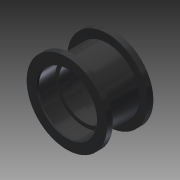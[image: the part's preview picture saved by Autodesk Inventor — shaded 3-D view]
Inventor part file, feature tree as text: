
AUTODESK INVENTOR PART (.ipt)
format: ipt  version: 2014 SP1 (Build 180222100, 222)  size: 124,416 bytes
history: native  units: in
note: dims shown in document units (in); Inventor stores cm internally (conversion verified against a paired STEP export)
features: revolve x1, chamfer x1, sketch x1
ambient origin geometry x8: Origin, YZ Plane, XZ Plane, XY Plane, X Axis, Y Axis, Z Axis, Center Point
bodies: Solid1 (feature_tree)
feature tree (3):
  revolve  "Revolution1"  [1 undecoded]
  chamfer  "Chamfer1"  Distance=0.5469in
  sketch  "Sketch1"  dims[d0=0.374in d1=0.6289in d2=0.5469in d3=0.122in d4=0.5in d5=0.689in d6=0.8661in d7=90.0deg d8=0.0118in d9=0.125in d10=45.0deg]
note: 1 required parameter value undecoded (feature->parameter linkage not recoverable at this tier; creation-order binding heuristic only, values carry confidence <= 0.55)
